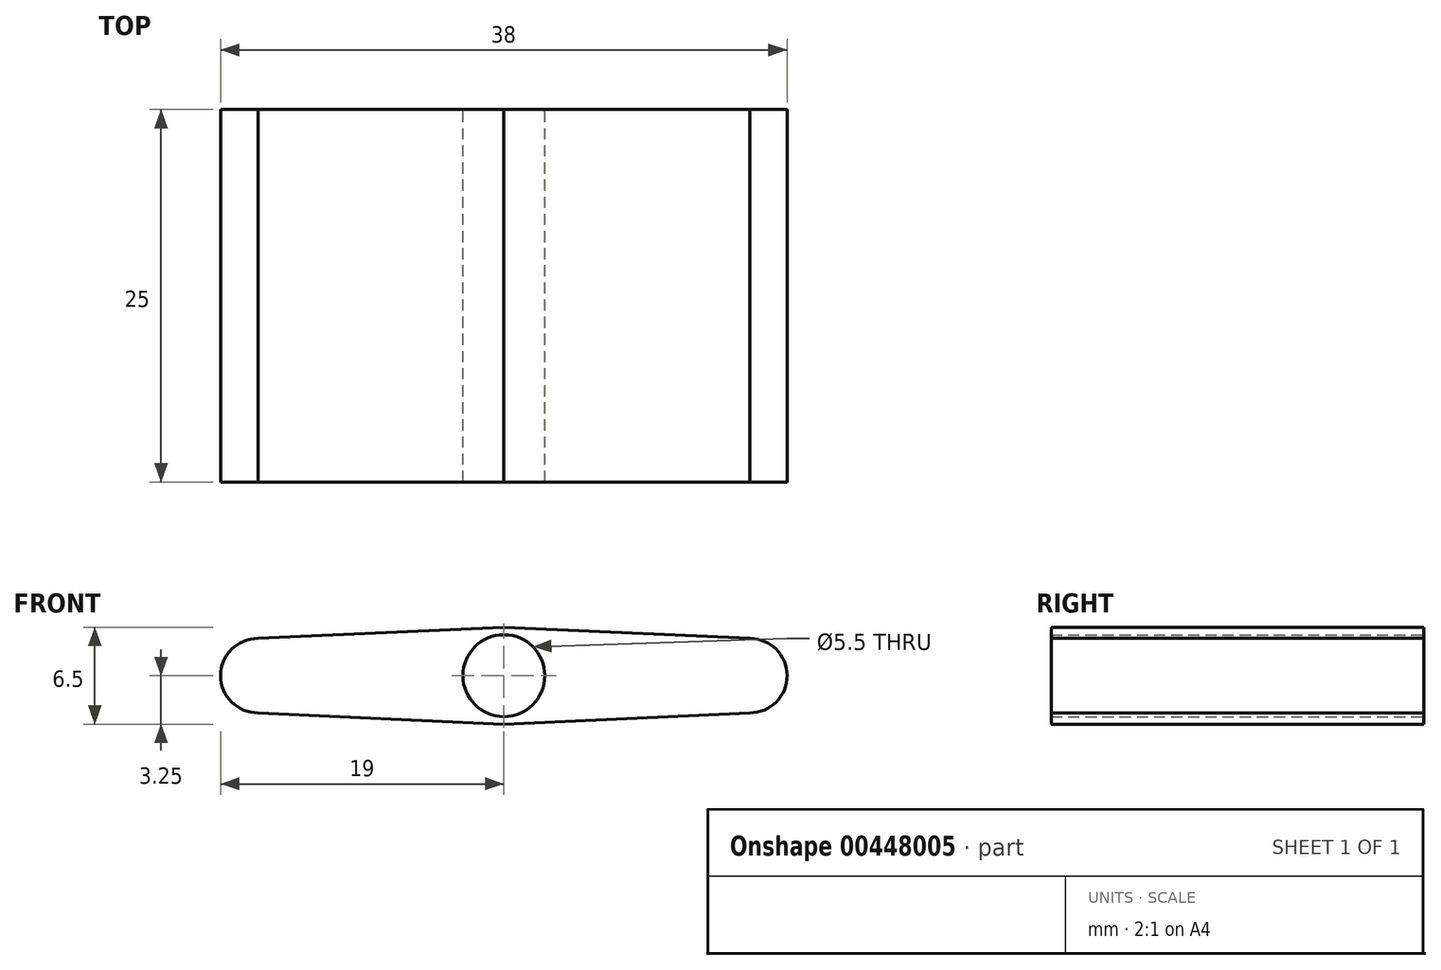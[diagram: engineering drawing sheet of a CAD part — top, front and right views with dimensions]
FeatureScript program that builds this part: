
annotation { "Feature Type Name" : "Feature", "Feature Type Description" : "" }
export const myFeature = defineFeature(function(context is Context, id is Id, definition is map)
    precondition{}
    {
        {
            var Q0;
            Q0=qCreatedBy(makeId("Front.planeOp"),FACE);
            var sketch = newSketch(context, id + "F0", { "sketchPlane" : qUnion([Q0])});
            skLineSegment(sketch, "E0.left", {"start": v(-16.5, 2.5) * mm, "end": v(-16.5, -2.5) * mm});
            skLineSegment(sketch, "E0.right", {"start": v(16.5, 2.5) * mm, "end": v(16.5, -2.5) * mm});
            skCircle(sketch, "E1", {"center": v(0, 0) * mm, "radius": 2.75 * mm});
            skArc(sketch, "E2", {"start": v(-16.5, 2.5) * mm, "mid": v(-19, 0) * mm, "end": v(-16.5, -2.5) * mm});
            skArc(sketch, "E3", {"start": v(16.5, -2.5) * mm, "mid": v(19, 0) * mm, "end": v(16.5, 2.5) * mm});
            skLineSegment(sketch, "E4", {"start": v(-16.5, -2.5) * mm, "end": v(0, -3.25) * mm});
            skLineSegment(sketch, "E5", {"start": v(0, -3.25) * mm, "end": v(16.5, -2.5) * mm});
            skLineSegment(sketch, "E6", {"start": v(16.5, 2.5) * mm, "end": v(0, 3.25) * mm});
            skLineSegment(sketch, "E7", {"start": v(0, 3.25) * mm, "end": v(-16.5, 2.5) * mm});
            skSolve(sketch);
        }
        {
            var Q0;
            Q0 = qSketchRegion(id + "F0", true);
            extrude(context, id + "F1", {"entities" : qUnion([Q0]), "depth" : 25 * mm});
        }
        {
            var Q0;
            {var subQ2=sQuery(id+"F0.wireOp",EDGE,"E1");var subQ8=sQuery(id+"F0.wireOp",EDGE,"6XHvpfAx-2tKT-LaVR-n82s-EbX0efgZk50R");var subQ9=makeQuery(id+"F0.imprint","INTERSECT",VERTEX,{"derivedFrom":[subQ2,subQ8]});Q0=makeQuery(id+"F0.imprint","IMPRINT",FACE,{"disambiguationData":[TD([[makeQuery(id+"F0.imprint","IMPRINT",EDGE,{"disambiguationData":[TD([[subQ9,-1.0]])],"derivedFrom":subQ2}),1.0]])]});}
            extrude(context, id + "F2", {"entities" : qUnion([Q0]), "operationType" : NewBodyOperationType.REMOVE, "depth" : 25 * mm});
        }
    });
